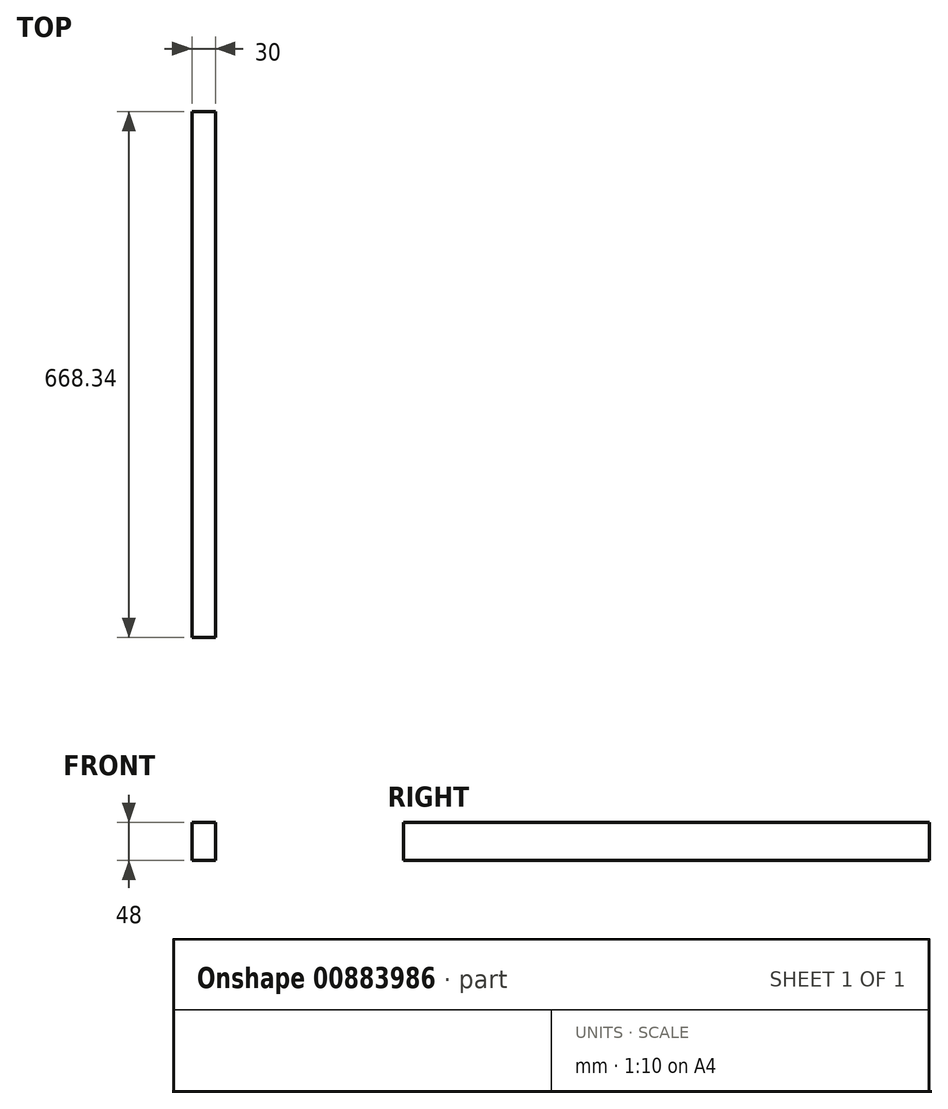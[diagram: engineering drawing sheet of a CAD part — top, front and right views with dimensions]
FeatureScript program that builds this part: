
annotation { "Feature Type Name" : "Feature", "Feature Type Description" : "" }
export const myFeature = defineFeature(function(context is Context, id is Id, definition is map)
    precondition{}
    {
        {
            var Q0;
            Q0=qCreatedBy(makeId("Top.planeOp"),FACE);
            var sketch = newSketch(context, id + "F0", { "sketchPlane" : qUnion([Q0])});
            skLineSegment(sketch, "E0.bottom", {"start": v(15, 334.17) * mm, "end": v(-15, 334.17) * mm});
            skLineSegment(sketch, "E0.top", {"start": v(15, -334.17) * mm, "end": v(-15, -334.17) * mm});
            skLineSegment(sketch, "E0.left", {"start": v(15, 334.17) * mm, "end": v(15, -334.17) * mm});
            skLineSegment(sketch, "E0.right", {"start": v(-15, 334.17) * mm, "end": v(-15, -334.17) * mm});
            skPoint(sketch, "E0.middle", {"position": v(0, 0) * mm});
            skSolve(sketch);
        }
        {
            var Q0;
            Q0=makeQuery(id+"F0.imprint","IMPRINT",FACE,{"disambiguationData":[TD([[makeQuery(id+"F0.imprint","IMPRINT",EDGE,{"derivedFrom":sQuery(id+"F0.wireOp",EDGE,"E0.bottom")}),1.0]])]});
            extrude(context, id + "F1", {"entities" : qUnion([Q0]), "oppositeDirection" : true, "depth" : 48 * mm, "offsetDistance" : 25 * mm});
        }
    });
